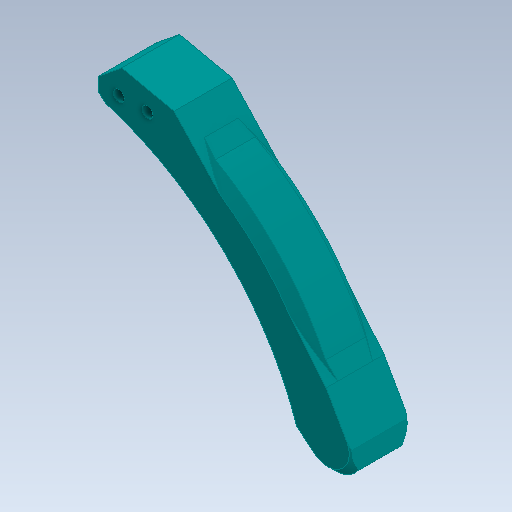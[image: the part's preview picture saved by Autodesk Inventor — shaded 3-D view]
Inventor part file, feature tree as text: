
AUTODESK INVENTOR PART (.ipt)
format: ipt  version: 2020 (Build 240168000, 168)  size: 215,040 bytes
history: native  units: in
note: dims shown in document units (in); Inventor stores cm internally (conversion verified against a paired STEP export)
features: chamfer x6, extrude x2, sketch x2, projected_geometry x1
ambient origin geometry x8: Origin, YZ Plane, XZ Plane, XY Plane, X Axis, Y Axis, Z Axis, Center Point
bodies: Solid1 (feature_tree)
feature tree (11):
  extrude  "Extrusion1"  Depth=0.315in
  extrude  "Extrusion2"  Depth=0.315in
  chamfer  "Chamfer2"  Distance=0.1575in
  chamfer  "Chamfer3"  Distance=0.1575in
  chamfer  "Chamfer4"  Distance=0.7027in
  chamfer  "Chamfer5"  Distance=0.7082in
  chamfer  "Chamfer6"  Distance=0.5906in
  chamfer  "Chamfer7"  Distance=0.5906in
  sketch  "Sketch1"  dims[d0=0.1181in d1=0.315in]
  sketch  "Sketch2"  dims[d2=0.1181in d3=0.2953in d4=0.1575in d5=0.1575in d6=0.7027in d7=0.7082in d8=0.5906in d9=0.5906in d10=0.315in d11=0.6378in d12=0.0in d13=0.3937in d14=60.0deg d15=0.3937in d17=1.9685in d18=2.9528in d19=1.9685in d20=2.9528in d24=0.6378in d25=0.0in d29=0.5906in d30=0.4331in d31=0.315in d32=0.9734in d33=0.2362in d34=0.0787in d35=45.0deg d36=0.0984in d37=0.0787in d38=45.0deg d39=0.3346in d40=0.0787in d41=45.0deg d42=0.0787in d43=0.0787in d44=45.0deg d45=0.1181in d46=0.0787in d47=45.0deg d48=0.1181in d49=0.0787in d50=45.0deg]
  projected_geometry  "Projected Loop1"
